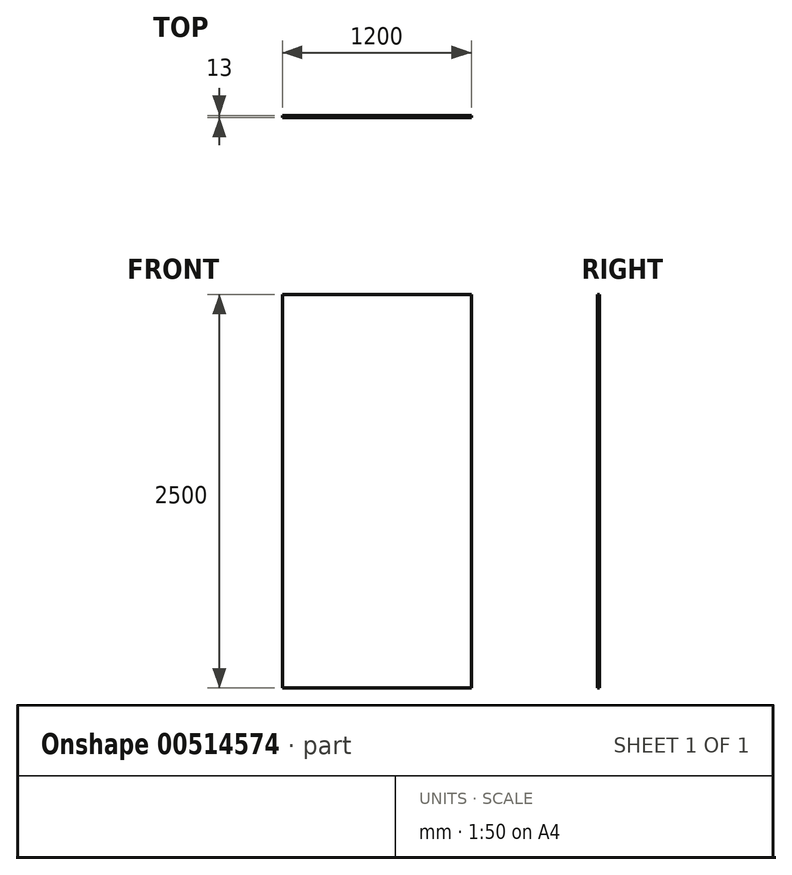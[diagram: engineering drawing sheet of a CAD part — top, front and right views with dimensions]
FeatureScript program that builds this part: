
annotation { "Feature Type Name" : "Feature", "Feature Type Description" : "" }
export const myFeature = defineFeature(function(context is Context, id is Id, definition is map)
    precondition{}
    {
        {
            var Q0;
            Q0=qCreatedBy(makeId("Front.planeOp"),FACE);
            var sketch = newSketch(context, id + "F0", { "sketchPlane" : qUnion([Q0])});
            skLineSegment(sketch, "E0.bottom", {"start": v(-600, 1250) * mm, "end": v(600, 1250) * mm});
            skLineSegment(sketch, "E0.top", {"start": v(-600, -1250) * mm, "end": v(600, -1250) * mm});
            skLineSegment(sketch, "E0.left", {"start": v(-600, 1250) * mm, "end": v(-600, -1250) * mm});
            skLineSegment(sketch, "E0.right", {"start": v(600, 1250) * mm, "end": v(600, -1250) * mm});
            skPoint(sketch, "E0.middle", {"position": v(0, 0) * mm});
            skSolve(sketch);
        }
        {
            var Q0;
            Q0 = qSketchRegion(id + "F0", true);
            extrude(context, id + "F1", {"entities" : qUnion([Q0]), "depth" : 13 * mm, "offsetDistance" : 25 * mm});
        }
    });
